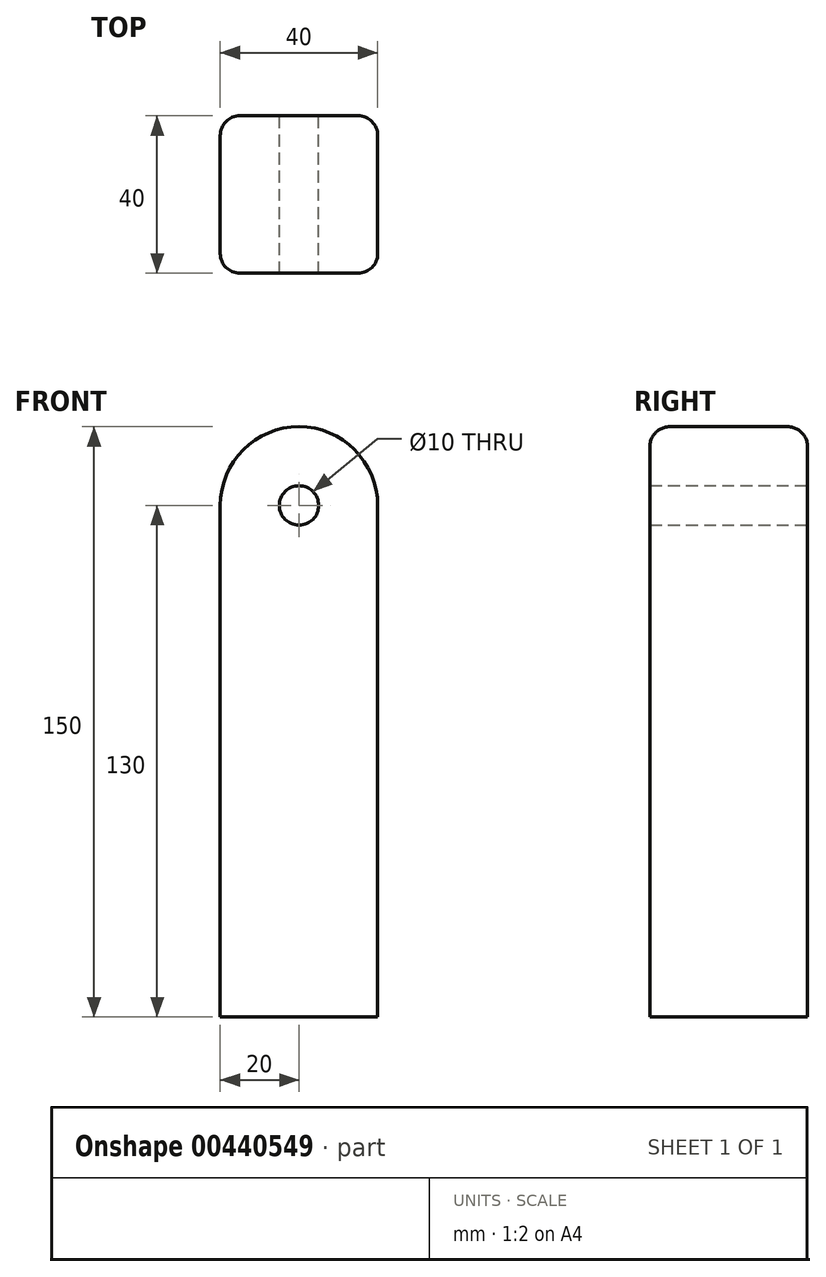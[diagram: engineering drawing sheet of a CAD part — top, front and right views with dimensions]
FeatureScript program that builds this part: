
annotation { "Feature Type Name" : "Feature", "Feature Type Description" : "" }
export const myFeature = defineFeature(function(context is Context, id is Id, definition is map)
    precondition{}
    {
        {
            var Q0;
            Q0=qCreatedBy(makeId("Front.planeOp"),FACE);
            var sketch = newSketch(context, id + "F0", { "sketchPlane" : qUnion([Q0])});
            skLineSegment(sketch, "E0.bottom", {"start": v(0, 75) * mm, "end": v(0, 75) * mm});
            skLineSegment(sketch, "E0.top", {"start": v(-20, -75) * mm, "end": v(20, -75) * mm});
            skLineSegment(sketch, "E0.left", {"start": v(-20, 55) * mm, "end": v(-20, -75) * mm});
            skLineSegment(sketch, "E0.right", {"start": v(20, 55) * mm, "end": v(20, -75) * mm});
            skPoint(sketch, "E0.middle", {"position": v(0, 0) * mm});
            skPoint(sketch, "E1.visualSharp", {"position": v(-20, 75) * mm});
            skArc(sketch, "E1.filletArc", {"start": v(0, 75) * mm, "mid": v(-14.14, 69.14) * mm, "end": v(-20, 55) * mm});
            skPoint(sketch, "E2.visualSharp", {"position": v(20, 75) * mm});
            skArc(sketch, "E2.filletArc", {"start": v(20, 55) * mm, "mid": v(14.14, 69.14) * mm, "end": v(0, 75) * mm});
            skSolve(sketch);
        }
        {
            var Q0;
            Q0=makeQuery(id+"F0.imprint","IMPRINT",FACE,{"disambiguationData":[TD([[makeQuery(id+"F0.imprint","IMPRINT",EDGE,{"derivedFrom":sQuery(id+"F0.wireOp",EDGE,"E0.top")}),1.0]])]});
            extrude(context, id + "F1", {"entities" : qUnion([Q0]), "depth" : 40 * mm});
        }
        {
            var Q0;
            Q0=sQuery(id+"F0.wireOp",VERTEX,"E1.filletArc.center");
            var Q1;
            Q1=makeQuery(id+"F1.opExtrude","SWEPT_BODY",BODY,{"disambiguationData":[OSD([sQuery(id+"F0.wireOp",EDGE,"E0.top"),sQuery(id+"F0.wireOp",EDGE,"E0.left"),sQuery(id+"F0.wireOp",EDGE,"E0.right"),sQuery(id+"F0.wireOp",EDGE,"E1.filletArc"),sQuery(id+"F0.wireOp",EDGE,"E2.filletArc")])]});
            hole(context, id + "F2", {"style" : HoleStyle.SIMPLE, "endStyle" : HoleEndStyle.THROUGH, "oppositeDirection" : true, "holeDiameter" : 10 * mm, "isTappedThrough" : true, "tappedDepth" : 12 * mm, "tapClearance" : 3, "startFromSketch" : true, "locations" : qUnion([Q0]), "scope" : qUnion([Q1])});
        }
        {
            var Q0;
            Q0=makeQuery(id+"F1.opExtrude","CAP_EDGE",EDGE,{"disambiguationData":[OSD([sQuery(id+"F0.wireOp",EDGE,"E1.filletArc"),sQuery(id+"F0.wireOp",EDGE,"E2.filletArc")])],"isStart":false});
            var Q1;
            Q1=makeQuery(id+"F1.opExtrude","CAP_EDGE",EDGE,{"disambiguationData":[OSD([sQuery(id+"F0.wireOp",EDGE,"E1.filletArc"),sQuery(id+"F0.wireOp",EDGE,"E2.filletArc")])],"isStart":true});
            fillet(context, id + "F3", {"entities" : qUnion([Q0, Q1]), "radius" : 5 * mm, "tangentPropagation" : true, "allowEdgeOverflow" : false});
        }
    });
